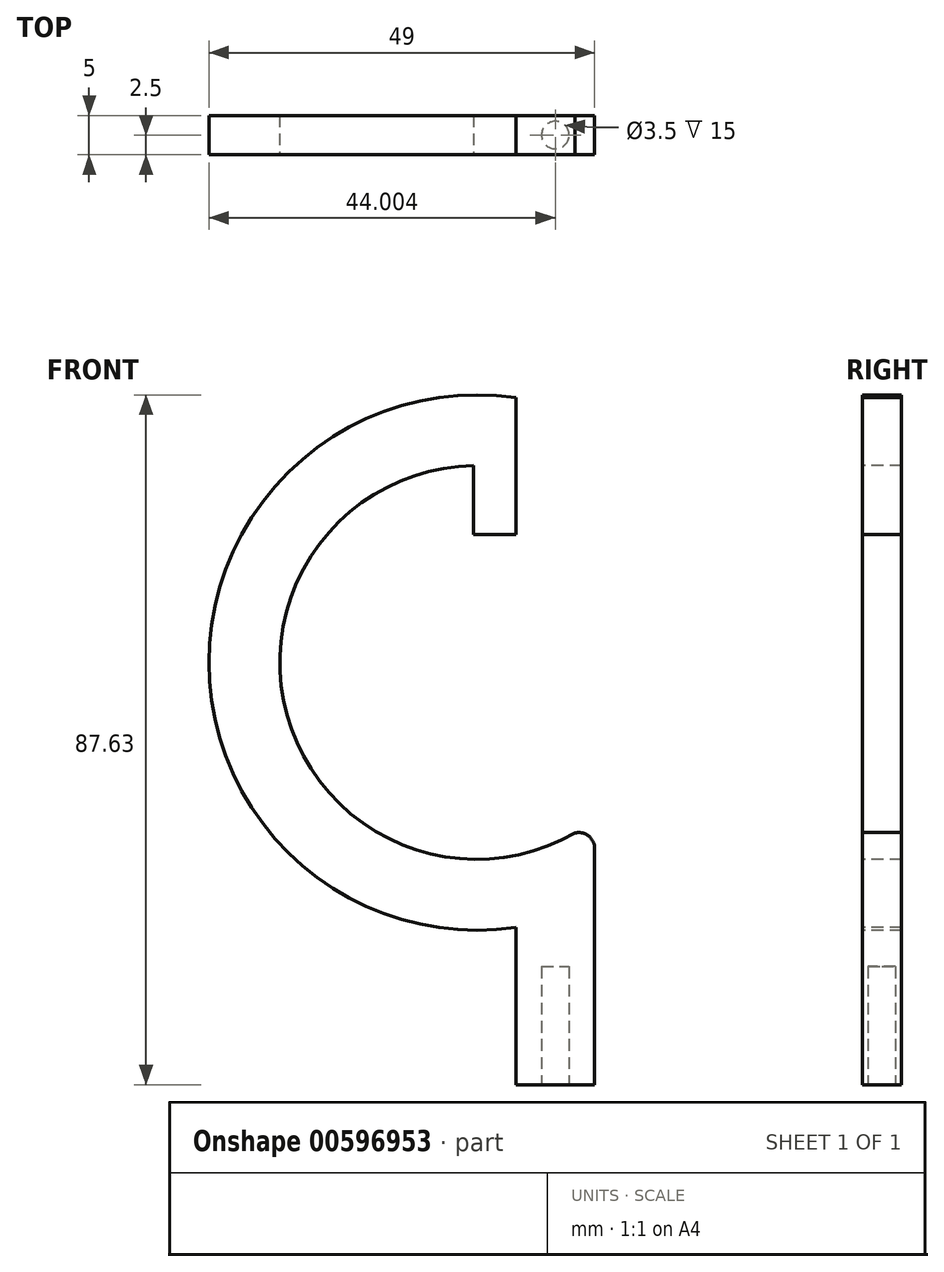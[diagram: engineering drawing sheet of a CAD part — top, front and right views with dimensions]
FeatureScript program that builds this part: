
annotation { "Feature Type Name" : "Feature", "Feature Type Description" : "" }
export const myFeature = defineFeature(function(context is Context, id is Id, definition is map)
    precondition{}
    {
        {
            var Q0;
            Q0=qCreatedBy(makeId("Front.planeOp"),FACE);
            var sketch = newSketch(context, id + "F0", { "sketchPlane" : qUnion([Q0])});
            skArc(sketch, "E0", {"start": v(-33.63, 55.79) * mm, "mid": v(-72.63, 22.16) * mm, "end": v(-33.63, -11.47) * mm});
            skPoint(sketch, "E1.start.orphan", {"position": v(-33.63, 22.16) * mm});
            skLineSegment(sketch, "E2", {"start": v(-33.63, -11.47) * mm, "end": v(-33.63, -31.47) * mm});
            skLineSegment(sketch, "E3", {"start": v(-33.63, -31.47) * mm, "end": v(-23.63, -31.47) * mm});
            skLineSegment(sketch, "E4", {"start": v(-23.63, -31.47) * mm, "end": v(-23.63, -1.47) * mm});
            skArc(sketch, "E5", {"start": v(-39, 47.16) * mm, "mid": v(-62.73, 15.52) * mm, "end": v(-26.15, 0.5) * mm});
            skPoint(sketch, "E6.start.orphan", {"position": v(-28.63, 22.16) * mm});
            skArc(sketch, "E7", {"start": v(-23.63, -1.47) * mm, "mid": v(-24.85, 0.4) * mm, "end": v(-27.05, 0) * mm});
            skPoint(sketch, "E8.centerSnap0", {"position": v(-28.63, -31.47) * mm});
            skCircle(sketch, "E9", {"center": v(-28.63, -35.48) * mm, "radius": 1.75 * mm});
            skLineSegment(sketch, "E10", {"start": v(-39, 47.16) * mm, "end": v(-39, 38.44) * mm});
            skLineSegment(sketch, "E11", {"start": v(-33.63, 55.79) * mm, "end": v(-33.63, 38.44) * mm});
            skLineSegment(sketch, "E12", {"start": v(-33.63, 38.44) * mm, "end": v(-39, 38.44) * mm});
            skSolve(sketch);
        }
        {
            var Q0;
            Q0=makeQuery(id+"F0.imprint","IMPRINT",FACE,{"disambiguationData":[TD([[makeQuery(id+"F0.imprint","IMPRINT",EDGE,{"derivedFrom":sQuery(id+"F0.wireOp",EDGE,"E0")}),1.0]])]});
            extrude(context, id + "F1", {"entities" : qUnion([Q0]), "oppositeDirection" : true, "depth" : 5 * mm, "offsetDistance" : 25 * mm});
        }
        {
            var Q0;
            Q0=makeQuery(id+"F1.opExtrude","SWEPT_FACE",FACE,{"disambiguationData":[OSD([sQuery(id+"F0.wireOp",EDGE,"E3")])]});
            var sketch = newSketch(context, id + "F2", { "sketchPlane" : qUnion([Q0])});
            skCircle(sketch, "E13", {"center": v(-28.63, -2.5) * mm, "radius": 1.75 * mm});
            skPoint(sketch, "E14.start.orphan", {"position": v(-28.63, 0) * mm});
            skPoint(sketch, "E15.trimOffspring.end.orphan", {"position": v(-28.63, -5) * mm});
            skPoint(sketch, "E16.orphan", {"position": v(-23.63, -2.5) * mm});
            skPoint(sketch, "E17.start.orphan", {"position": v(-33.63, -2.5) * mm});
            skSolve(sketch);
        }
        {
            var Q0;
            Q0=makeQuery(id+"F2.imprint","IMPRINT",FACE,{"disambiguationData":[TD([[makeQuery(id+"F2.imprint","IMPRINT",EDGE,{"derivedFrom":sQuery(id+"F2.wireOp",EDGE,"E13")}),1.0]])]});
            extrude(context, id + "F3", {"entities" : qUnion([Q0]), "operationType" : NewBodyOperationType.REMOVE, "oppositeDirection" : true, "depth" : 15 * mm, "offsetDistance" : 25 * mm});
        }
    });
